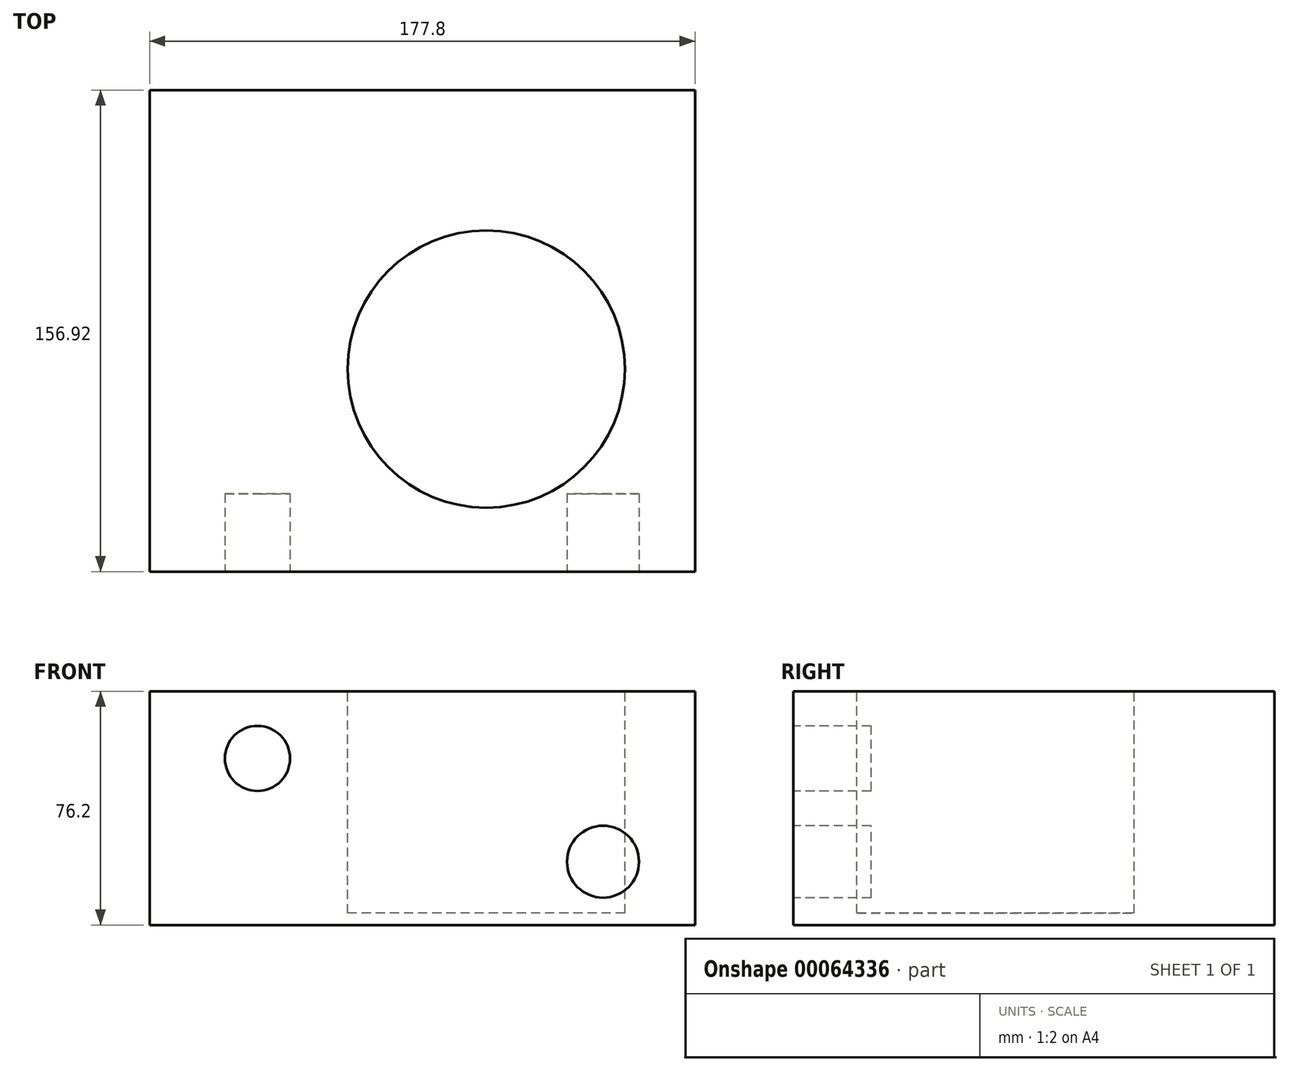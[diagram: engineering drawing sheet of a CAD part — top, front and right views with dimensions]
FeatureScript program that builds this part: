
annotation { "Feature Type Name" : "Feature", "Feature Type Description" : "" }
export const myFeature = defineFeature(function(context is Context, id is Id, definition is map)
    precondition{}
    {
        {
            var Q0;
            Q0=qCreatedBy(makeId("Front.planeOp"),FACE);
            var sketch = newSketch(context, id + "F0", { "sketchPlane" : qUnion([Q0])});
            skLineSegment(sketch, "E0.bottom", {"start": v(-21.63, 0) * mm, "end": v(156.17, 0) * mm});
            skLineSegment(sketch, "E0.top", {"start": v(-21.63, 76.2) * mm, "end": v(156.17, 76.2) * mm});
            skLineSegment(sketch, "E0.left", {"start": v(-21.63, 0) * mm, "end": v(-21.63, 76.2) * mm});
            skLineSegment(sketch, "E0.right", {"start": v(156.17, 0) * mm, "end": v(156.17, 76.2) * mm});
            skSolve(sketch);
        }
        {
            var Q0;
            Q0 = qSketchRegion(id + "F0", true);
            extrude(context, id + "F5", {"entities" : qUnion([Q0]), "depth" : 156.92 * mm});
        }
        {
            var Q0;
            Q0=makeQuery(id+"F5.opExtrude","SWEPT_FACE",FACE,{"disambiguationData":[OSD([sQuery(id+"F0.wireOp",EDGE,"E0.top")])]});
            var sketch = newSketch(context, id + "F1", { "sketchPlane" : qUnion([Q0])});
            skCircle(sketch, "E1", {"center": v(88.1, -90.91) * mm, "radius": 45.2 * mm});
            skSolve(sketch);
        }
        {
            var Q0;
            Q0 = qSketchRegion(id + "F1", true);
            extrude(context, id + "F2", {"entities" : qUnion([Q0]), "operationType" : NewBodyOperationType.REMOVE, "oppositeDirection" : true, "depth" : 72.34 * mm});
        }
        {
            var Q0;
            Q0=makeQuery(id+"F5.opExtrude","CAP_FACE",FACE,{"disambiguationData":[OSD([sQuery(id+"F0.wireOp",EDGE,"E0.bottom"),sQuery(id+"F0.wireOp",EDGE,"E0.top"),sQuery(id+"F0.wireOp",EDGE,"E0.left"),sQuery(id+"F0.wireOp",EDGE,"E0.right")])],"isStart":false});
            var sketch = newSketch(context, id + "F3", { "sketchPlane" : qUnion([Q0])});
            skCircle(sketch, "E2", {"center": v(13.54, 54.28) * mm, "radius": 10.62 * mm});
            skCircle(sketch, "E3", {"center": v(126.18, 20.62) * mm, "radius": 11.72 * mm});
            skSolve(sketch);
        }
        {
            var Q0;
            Q0=makeQuery(id+"F3.imprint","IMPRINT",FACE,{"disambiguationData":[TD([[makeQuery(id+"F3.imprint","IMPRINT",EDGE,{"derivedFrom":sQuery(id+"F3.wireOp",EDGE,"E2")}),1.0]])]});
            var Q1;
            Q1=makeQuery(id+"F3.imprint","IMPRINT",FACE,{"disambiguationData":[TD([[makeQuery(id+"F3.imprint","IMPRINT",EDGE,{"derivedFrom":sQuery(id+"F3.wireOp",EDGE,"E3")}),1.0]])]});
            extrude(context, id + "F4", {"entities" : qUnion([Q0, Q1]), "operationType" : NewBodyOperationType.REMOVE, "oppositeDirection" : true, "depth" : 25.4 * mm});
        }
    });
